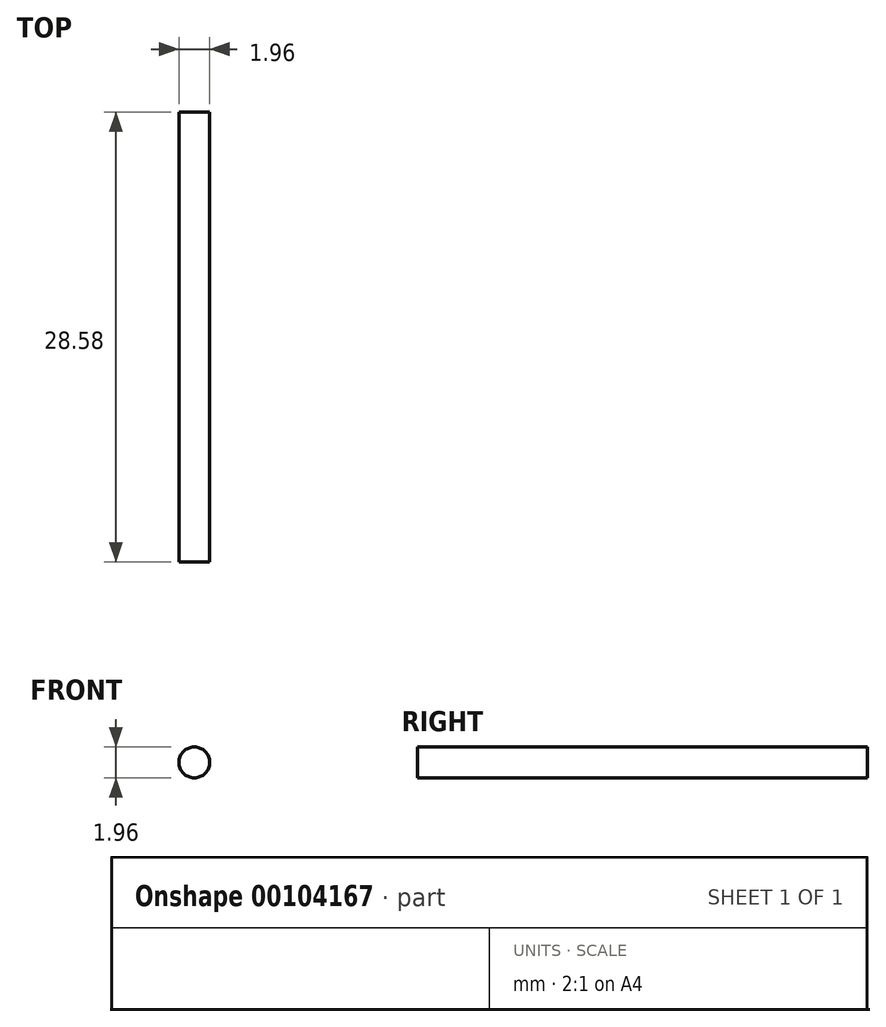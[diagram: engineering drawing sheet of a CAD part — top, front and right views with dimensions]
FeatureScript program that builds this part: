
annotation { "Feature Type Name" : "Feature", "Feature Type Description" : "" }
export const myFeature = defineFeature(function(context is Context, id is Id, definition is map)
    precondition{}
    {
        {
            var Q0;
            Q0=qCreatedBy(makeId("Front.planeOp"),FACE);
            var sketch = newSketch(context, id + "F0", { "sketchPlane" : qUnion([Q0])});
            skCircle(sketch, "E0", {"center": v(-44.55, 9.56) * mm, "radius": 0.98 * mm});
            skSolve(sketch);
        }
        {
            var Q0;
            Q0=makeQuery(id+"F0.imprint","IMPRINT",FACE,{"disambiguationData":[TD([[makeQuery(id+"F0.imprint","IMPRINT",EDGE,{"derivedFrom":sQuery(id+"F0.wireOp",EDGE,"E0")}),1.0]])]});
            extrude(context, id + "F1", {"entities" : qUnion([Q0]), "depth" : 28.57 * mm});
        }
    });
